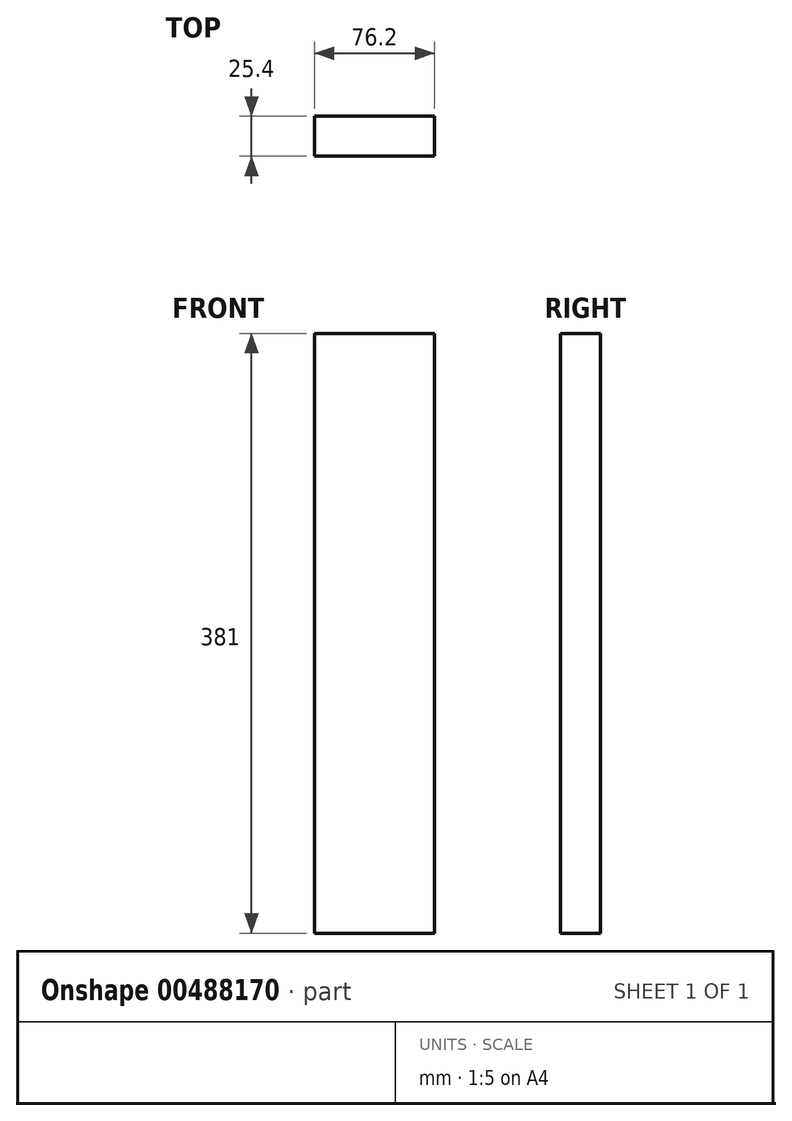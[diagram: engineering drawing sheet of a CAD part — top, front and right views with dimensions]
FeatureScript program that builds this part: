
annotation { "Feature Type Name" : "Feature", "Feature Type Description" : "" }
export const myFeature = defineFeature(function(context is Context, id is Id, definition is map)
    precondition{}
    {
        {
            var Q0;
            Q0=qCreatedBy(makeId("Front.planeOp"),FACE);
            var sketch = newSketch(context, id + "F0", { "sketchPlane" : qUnion([Q0])});
            skLineSegment(sketch, "E0", {"start": v(0, 0) * mm, "end": v(76.2, 0) * mm});
            skLineSegment(sketch, "E1", {"start": v(76.2, 0) * mm, "end": v(76.2, 381) * mm});
            skLineSegment(sketch, "E2", {"start": v(76.2, 381) * mm, "end": v(0, 381) * mm});
            skLineSegment(sketch, "E3", {"start": v(0, 381) * mm, "end": v(0, 0) * mm});
            skSolve(sketch);
        }
        {
            var Q0;
            Q0=makeQuery(id+"F0.imprint","IMPRINT",FACE,{"disambiguationData":[TD([[makeQuery(id+"F0.imprint","IMPRINT",EDGE,{"derivedFrom":sQuery(id+"F0.wireOp",EDGE,"E0")}),1.0]])]});
            extrude(context, id + "F1", {"entities" : qUnion([Q0]), "depth" : 25.4 * mm, "offsetDistance" : 25.4 * mm});
        }
    });
